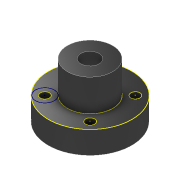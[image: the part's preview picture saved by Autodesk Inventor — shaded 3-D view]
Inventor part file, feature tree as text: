
AUTODESK INVENTOR PART (.ipt)
format: ipt  version: 2022 (Build 260153000, 153)  size: 142,336 bytes
history: native  units: mm
features: sketch x5, extrude x4, projected_geometry x1
ambient origin geometry x8: Origin, YZ Plane, XZ Plane, XY Plane, X Axis, Y Axis, Z Axis, Center Point
bodies: Solid1 (feature_tree)
feature tree (10):
  extrude  "Extrusion1"  Depth=10.0mm
  extrude  "Extrusion2"  Depth=8.0mm
  extrude  "Extrusion3"  Depth=7.0mm
  extrude  "Extrusion4"  Depth=4.0mm TaperAngle=0.0deg
  sketch  "Sketch5"
  sketch  "Sketch1"  dims[d0=10.0mm d1=0.0mm d2=20.0mm]
  sketch  "Sketch2"  dims[d3=14.0mm d4=0.0mm d5=8.0mm]
  sketch  "Sketch3"  dims[d6=14.0mm d7=0.0mm d8=7.0mm]
  sketch  "Sketch4"  dims[d9=4.0mm d10=14.0mm d11=0.0mm]
  projected_geometry  "Projected Loop1"
